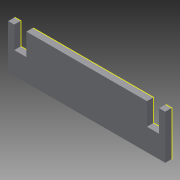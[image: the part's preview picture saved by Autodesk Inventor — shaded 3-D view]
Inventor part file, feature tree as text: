
AUTODESK INVENTOR PART (.ipt)
format: ipt  version: 2015 (Build 190159000, 159)  size: 113,664 bytes
history: native  units: mm
features: sketch x3, extrude x2
ambient origin geometry x8: Origin, YZ Plane, XZ Plane, XY Plane, X Axis, Y Axis, Z Axis, Center Point
bodies: Solid1 (feature_tree)
feature tree (5):
  extrude  "Extrusion1"  Depth=3.0mm TaperAngle=0.0deg
  extrude  "Extrusion2"  Depth=5.5mm
  sketch  "Sketch4"  dims[d7=10.0mm d8=30.0mm d9=3.0mm d10=0.0mm]
  sketch  "Sketch1"  dims[d0=71.0mm d1=3.0mm d2=0.0mm]
  sketch  "Sketch3"  dims[d5=20.0mm d6=5.5mm]
